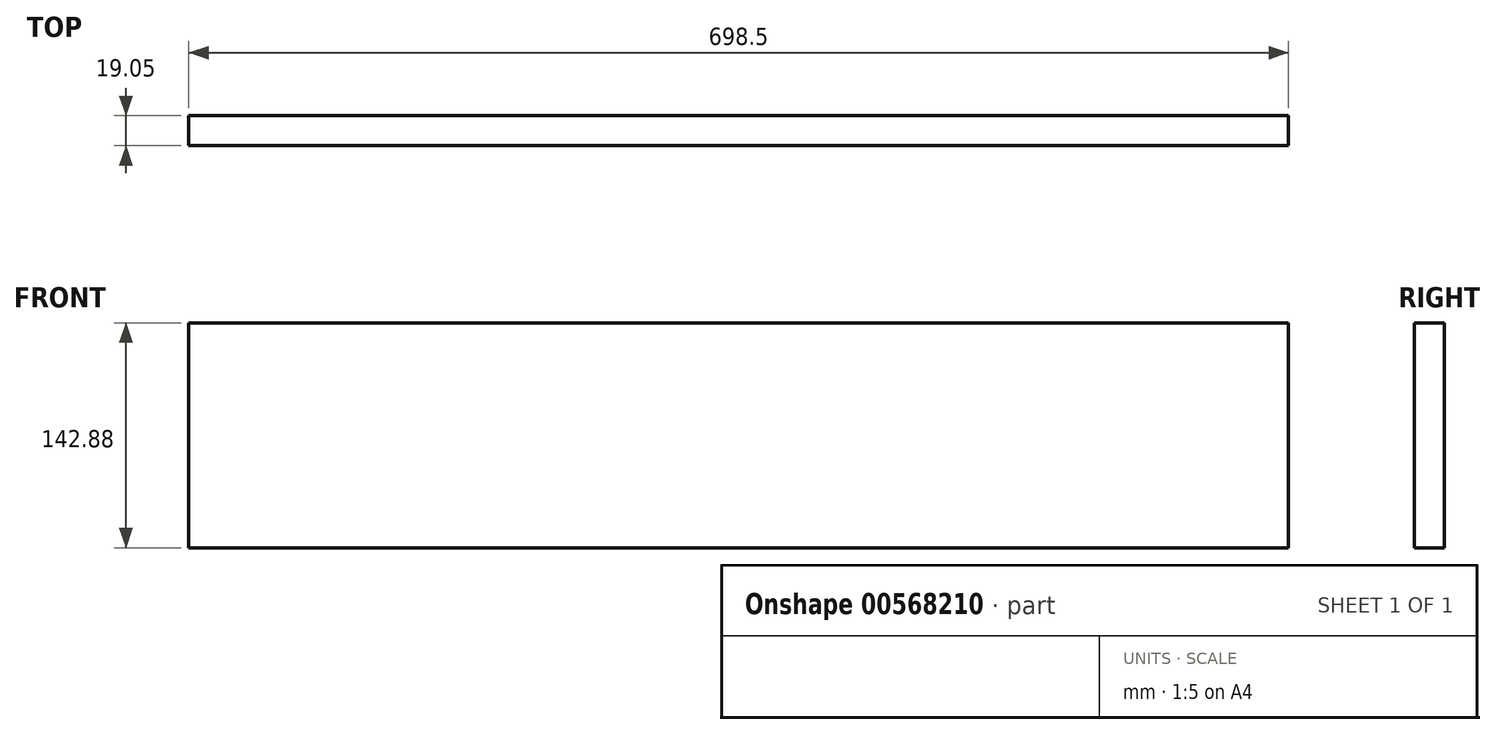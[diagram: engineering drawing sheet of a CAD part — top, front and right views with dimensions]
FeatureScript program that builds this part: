
annotation { "Feature Type Name" : "Feature", "Feature Type Description" : "" }
export const myFeature = defineFeature(function(context is Context, id is Id, definition is map)
    precondition{}
    {
        {
            var Q0;
            Q0=qCreatedBy(makeId("Front.planeOp"),FACE);
            var sketch = newSketch(context, id + "F0", { "sketchPlane" : qUnion([Q0])});
            skLineSegment(sketch, "E0.bottom", {"start": v(0, 0) * mm, "end": v(698.5, 0) * mm});
            skLineSegment(sketch, "E0.top", {"start": v(0, 142.88) * mm, "end": v(698.5, 142.88) * mm});
            skLineSegment(sketch, "E0.left", {"start": v(0, 0) * mm, "end": v(0, 142.88) * mm});
            skLineSegment(sketch, "E0.right", {"start": v(698.5, 0) * mm, "end": v(698.5, 142.88) * mm});
            skSolve(sketch);
        }
        {
            var Q0;
            Q0=makeQuery(id+"F0.imprint","IMPRINT",FACE,{"disambiguationData":[TD([[makeQuery(id+"F0.imprint","IMPRINT",EDGE,{"derivedFrom":sQuery(id+"F0.wireOp",EDGE,"E0.bottom")}),1.0]])]});
            extrude(context, id + "F1", {"entities" : qUnion([Q0]), "depth" : 19.05 * mm, "offsetDistance" : 25.4 * mm});
        }
    });
